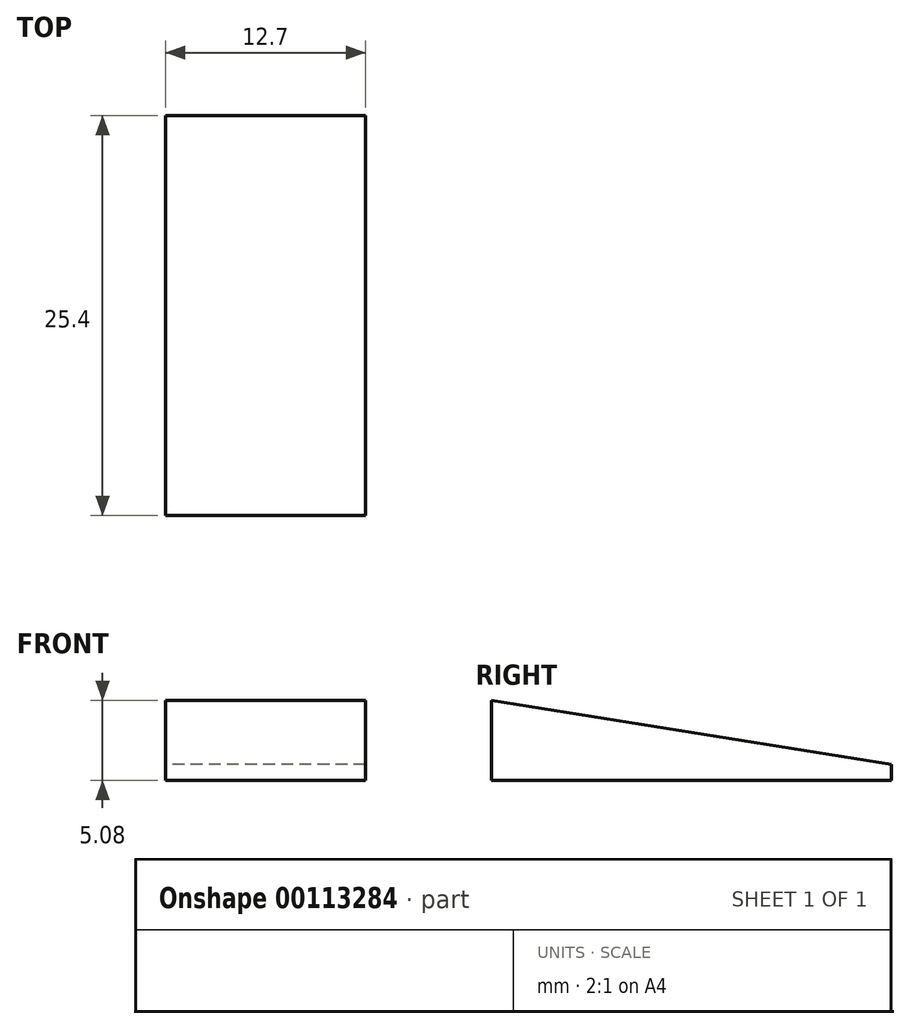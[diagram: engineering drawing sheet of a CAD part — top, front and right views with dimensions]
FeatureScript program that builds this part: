
annotation { "Feature Type Name" : "Feature", "Feature Type Description" : "" }
export const myFeature = defineFeature(function(context is Context, id is Id, definition is map)
    precondition{}
    {
        {
            var Q0;
            Q0=qCreatedBy(makeId("Right.planeOp"),FACE);
            var sketch = newSketch(context, id + "F0", { "sketchPlane" : qUnion([Q0])});
            skLineSegment(sketch, "E0", {"start": v(-11.3, 3.56) * mm, "end": v(-11.3, -1.52) * mm});
            skLineSegment(sketch, "E1", {"start": v(-11.3, -1.52) * mm, "end": v(14.1, -1.52) * mm});
            skLineSegment(sketch, "E2", {"start": v(14.1, -1.52) * mm, "end": v(14.1, -0.52) * mm});
            skLineSegment(sketch, "E3", {"start": v(14.1, -0.52) * mm, "end": v(-11.3, 3.56) * mm});
            skSolve(sketch);
        }
        {
            var Q0;
            Q0=makeQuery(id+"F0.imprint","IMPRINT",FACE,{"disambiguationData":[TD([[makeQuery(id+"F0.imprint","IMPRINT",EDGE,{"derivedFrom":sQuery(id+"F0.wireOp",EDGE,"E0")}),1.0]])]});
            extrude(context, id + "F1", {"entities" : qUnion([Q0]), "depth" : 12.7 * mm});
        }
    });
